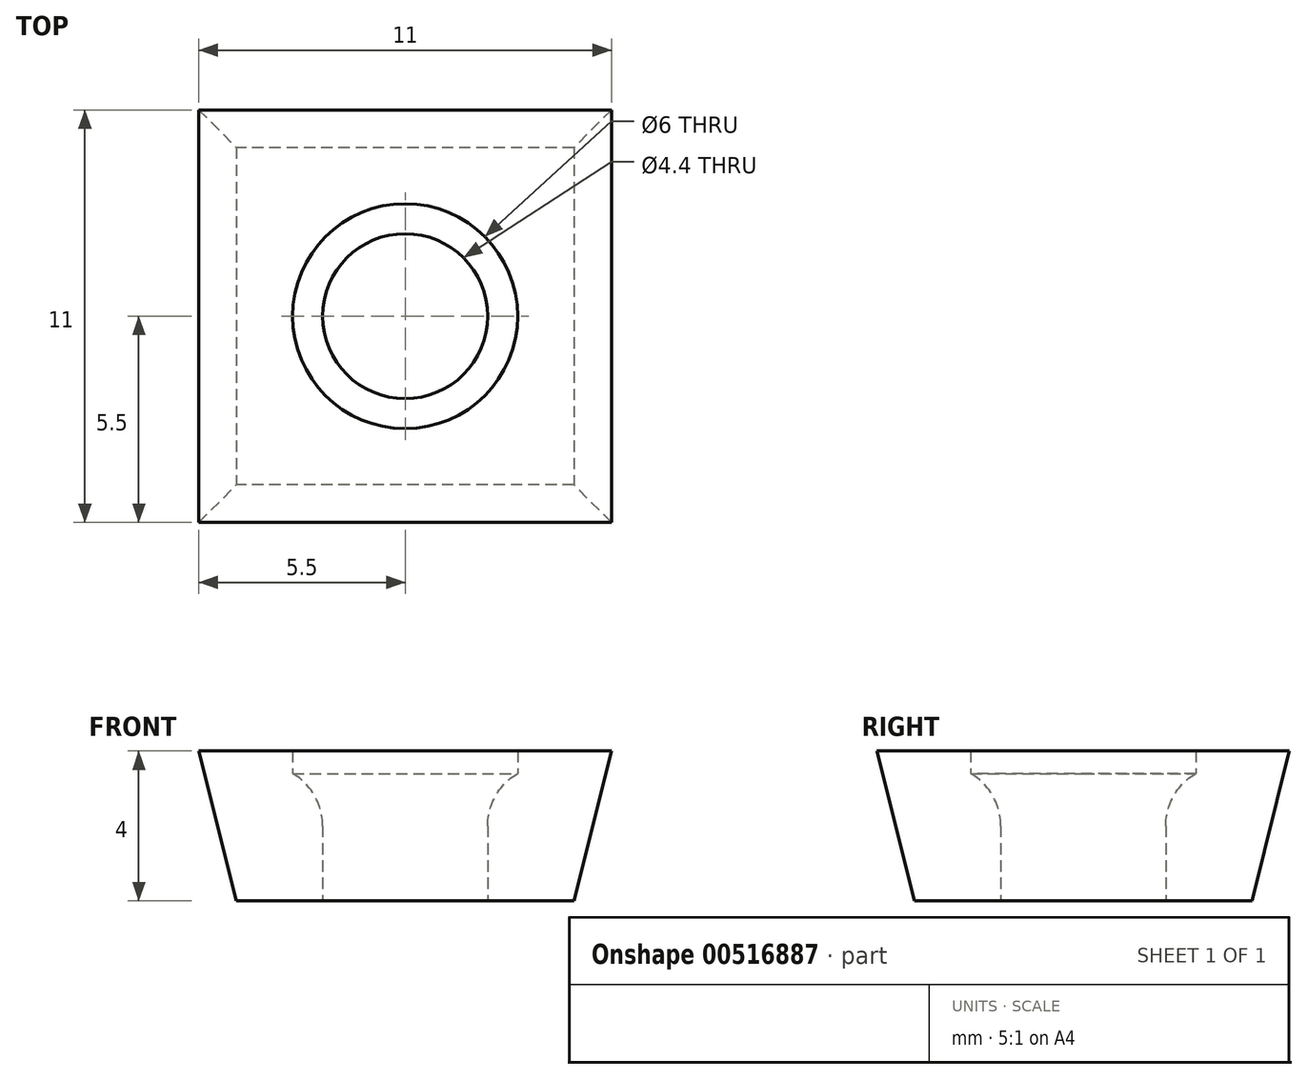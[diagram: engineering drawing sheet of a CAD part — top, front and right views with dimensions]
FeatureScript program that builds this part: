
annotation { "Feature Type Name" : "Feature", "Feature Type Description" : "" }
export const myFeature = defineFeature(function(context is Context, id is Id, definition is map)
    precondition{}
    {
        {
            var Q0;
            Q0=qCreatedBy(makeId("Top.planeOp"),FACE);
            var sketch = newSketch(context, id + "F0", { "sketchPlane" : qUnion([Q0])});
            skLineSegment(sketch, "E0.bottom", {"start": v(5.5, 5.5) * mm, "end": v(-5.5, 5.5) * mm});
            skLineSegment(sketch, "E0.top", {"start": v(5.5, -5.5) * mm, "end": v(-5.5, -5.5) * mm});
            skLineSegment(sketch, "E0.left", {"start": v(5.5, 5.5) * mm, "end": v(5.5, -5.5) * mm});
            skLineSegment(sketch, "E0.right", {"start": v(-5.5, 5.5) * mm, "end": v(-5.5, -5.5) * mm});
            skPoint(sketch, "E0.middle", {"position": v(0, 0) * mm});
            skSolve(sketch);
        }
        {
            var Q0;
            Q0=qCreatedBy(makeId("Top.planeOp"),FACE);
            cPlane(context, id + "F1", {"entities" : qUnion([Q0]), "cplaneType" : CPlaneType.OFFSET, "offset" : 4 * mm, "oppositeDirection" : true, "width" : 150 * mm, "height" : 150 * mm});
        }
        {
            var Q0;
            Q0=qCreatedBy(id+"F1.planeOp",FACE);
            var sketch = newSketch(context, id + "F2", { "sketchPlane" : qUnion([Q0])});
            skLineSegment(sketch, "E1.bottom", {"start": v(4.5, 4.5) * mm, "end": v(-4.5, 4.5) * mm});
            skLineSegment(sketch, "E1.top", {"start": v(4.5, -4.5) * mm, "end": v(-4.5, -4.5) * mm});
            skLineSegment(sketch, "E1.left", {"start": v(4.5, 4.5) * mm, "end": v(4.5, -4.5) * mm});
            skLineSegment(sketch, "E1.right", {"start": v(-4.5, 4.5) * mm, "end": v(-4.5, -4.5) * mm});
            skPoint(sketch, "E1.middle", {"position": v(0, 0) * mm});
            skSolve(sketch);
        }
        {
            var Q0;
            Q0=makeQuery(id+"F0.imprint","IMPRINT",FACE,{"disambiguationData":[TD([[makeQuery(id+"F0.imprint","IMPRINT",EDGE,{"derivedFrom":sQuery(id+"F0.wireOp",EDGE,"E0.bottom")}),1.0]])]});
            var Q1;
            Q1=makeQuery(id+"F2.imprint","IMPRINT",FACE,{"disambiguationData":[TD([[makeQuery(id+"F2.imprint","IMPRINT",EDGE,{"derivedFrom":sQuery(id+"F2.wireOp",EDGE,"E1.bottom")}),1.0]])]});
            loft(context, id + "F3", {"sheetProfilesArray" : [{ "sheetProfileEntities" : qUnion([Q0]) }, { "sheetProfileEntities" : qUnion([Q1]) }]});
        }
        {
            var Q0;
            Q0=qCreatedBy(makeId("Front.planeOp"),FACE);
            var sketch = newSketch(context, id + "F4", { "sketchPlane" : qUnion([Q0])});
            skLineSegment(sketch, "E2", {"start": v(0, 0.97) * mm, "end": v(0, -4.96) * mm, "construction": true});
            skLineSegment(sketch, "E3.0", {"start": v(4.5, -4) * mm, "end": v(0, -4) * mm});
            skLineSegment(sketch, "E4.0", {"start": v(5.5, 0) * mm, "end": v(0, 0) * mm});
            skLineSegment(sketch, "E5", {"start": v(2.2, -4) * mm, "end": v(2.2, -2) * mm});
            skLineSegment(sketch, "E6", {"start": v(3, 0) * mm, "end": v(3, -0.6) * mm});
            skArc(sketch, "E7", {"start": v(2.2, -2) * mm, "mid": v(2.41, -1.2) * mm, "end": v(3, -0.6) * mm});
            skLineSegment(sketch, "E8", {"start": v(0, 0) * mm, "end": v(0, -4) * mm});
            skPoint(sketch, "E9.orphan", {"position": v(-5.5, 0) * mm});
            skPoint(sketch, "E10.orphan", {"position": v(-4.5, -4) * mm});
            skSolve(sketch);
        }
        {
            var Q0;
            Q0=qSketchRegion(id+"F4",true);
            var Q1;
            Q1=sQuery(id+"F4.wireOp",EDGE,"E2");
            revolve(context, id + "F5", {"operationType" : NewBodyOperationType.REMOVE, "entities" : qUnion([Q0]), "axis" : qUnion([Q1]), "revolveType" : RevolveType.FULL, "oppositeDirection" : true});
        }
    });
